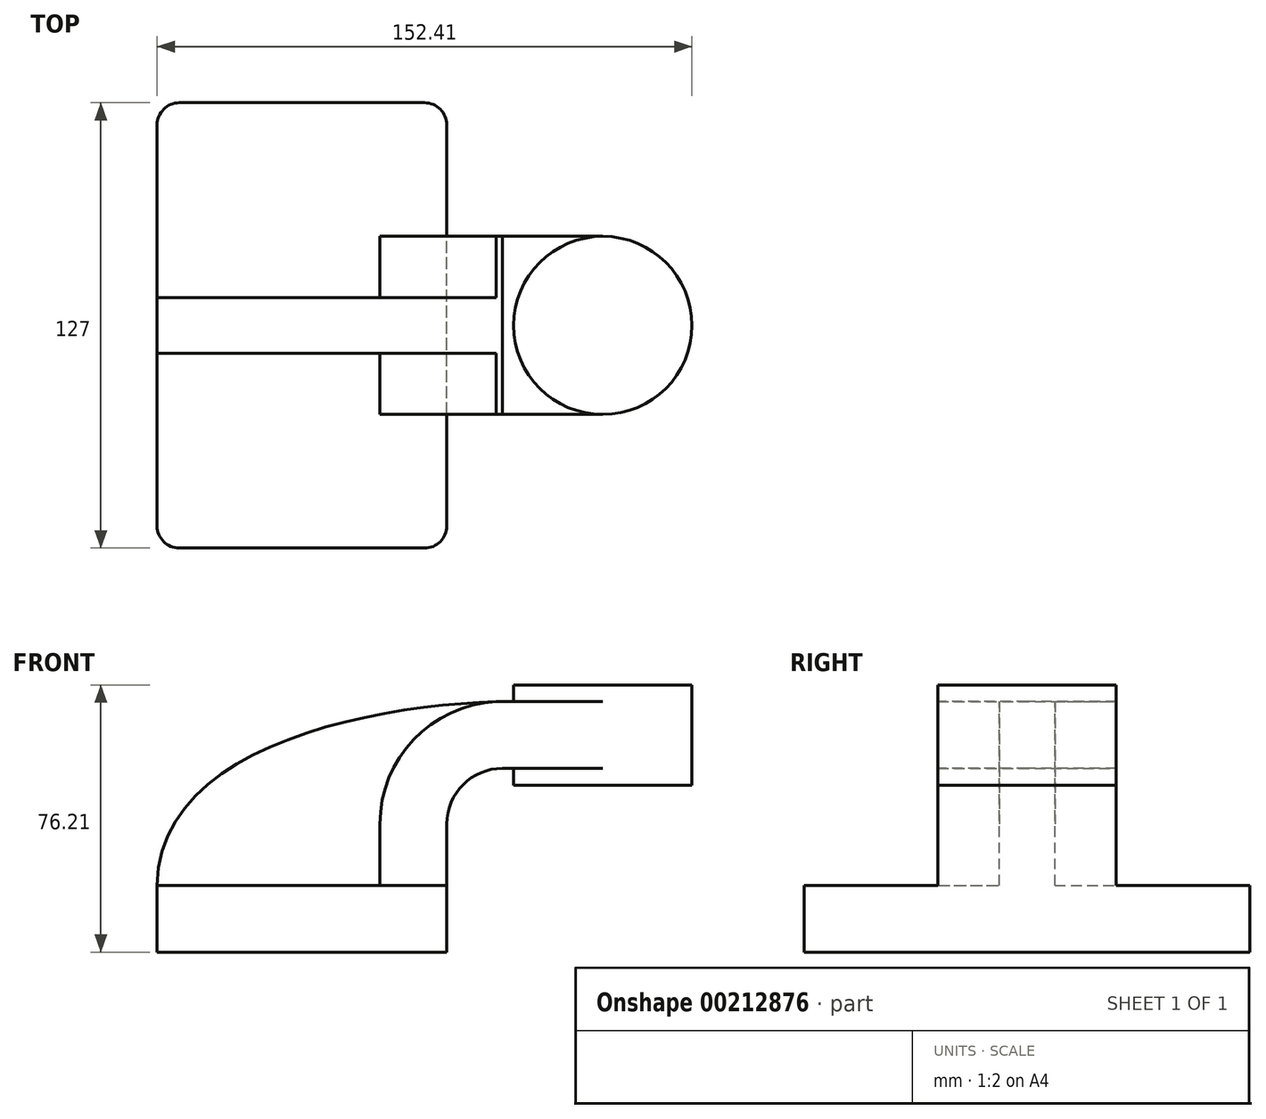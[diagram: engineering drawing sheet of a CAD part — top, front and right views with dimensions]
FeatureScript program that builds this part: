
annotation { "Feature Type Name" : "Feature", "Feature Type Description" : "" }
export const myFeature = defineFeature(function(context is Context, id is Id, definition is map)
    precondition{}
    {
        {
            var Q0;
            Q0=qCreatedBy(makeId("Front.planeOp"),FACE);
            var sketch = newSketch(context, id + "F0", { "sketchPlane" : qUnion([Q0])});
            skLineSegment(sketch, "E0.bottom", {"start": v(41.27, 9.53) * mm, "end": v(-41.28, 9.53) * mm});
            skLineSegment(sketch, "E0.top", {"start": v(41.28, -9.52) * mm, "end": v(-41.27, -9.52) * mm});
            skLineSegment(sketch, "E0.left", {"start": v(41.28, 9.53) * mm, "end": v(41.28, -9.52) * mm});
            skLineSegment(sketch, "E0.right", {"start": v(-41.28, 9.53) * mm, "end": v(-41.27, -9.52) * mm});
            skPoint(sketch, "E0.middle", {"position": v(0, 0) * mm});
            skLineSegment(sketch, "E1.bottom", {"start": v(111.12, 66.68) * mm, "end": v(60.32, 66.68) * mm});
            skLineSegment(sketch, "E1.top", {"start": v(111.13, 38.1) * mm, "end": v(60.32, 38.1) * mm});
            skLineSegment(sketch, "E1.left", {"start": v(111.12, 66.67) * mm, "end": v(111.13, 38.1) * mm});
            skLineSegment(sketch, "E1.right", {"start": v(60.32, 66.67) * mm, "end": v(60.32, 38.1) * mm});
            skPoint(sketch, "E1.middle", {"position": v(85.72, 52.39) * mm});
            skLineSegment(sketch, "E2", {"start": v(41.27, 9.53) * mm, "end": v(41.27, 27) * mm});
            skArc(sketch, "E3", {"start": v(41.27, 27) * mm, "mid": v(45.92, 38.23) * mm, "end": v(57.15, 42.88) * mm});
            skPoint(sketch, "E4.endSnap0", {"position": v(45.92, 38.23) * mm});
            skLineSegment(sketch, "E5", {"start": v(57.15, 42.88) * mm, "end": v(71.44, 42.88) * mm});
            skLineSegment(sketch, "E6.0", {"start": v(57.15, 61.93) * mm, "end": v(71.44, 61.93) * mm});
            skArc(sketch, "E6.1", {"start": v(22.23, 27) * mm, "mid": v(32.45, 51.7) * mm, "end": v(57.15, 61.93) * mm});
            skLineSegment(sketch, "E6.2", {"start": v(22.22, 9.53) * mm, "end": v(22.22, 27) * mm});
            skFitSpline(sketch, "E7", {"points": [v(-41.28, 9.52) * mm, v(57.15, 61.93) * mm], "startDerivative": vector(1.16, 119.88) * mm, "endDerivative": vector(109.6, 2.27) * mm});
            skLineSegment(sketch, "E8", {"start": v(85.72, 42.88) * mm, "end": v(85.72, 61.93) * mm});
            skLineSegment(sketch, "E9", {"start": v(71.44, 61.93) * mm, "end": v(85.72, 61.93) * mm});
            skLineSegment(sketch, "E10", {"start": v(71.44, 42.88) * mm, "end": v(85.72, 42.88) * mm});
            skLineSegment(sketch, "E11", {"start": v(85.72, 61.93) * mm, "end": v(85.72, 66.68) * mm});
            skLineSegment(sketch, "E12", {"start": v(85.72, 42.88) * mm, "end": v(85.72, 38.1) * mm});
            skSolve(sketch);
        }
        {
            var Q0;
            Q0=makeQuery(id+"F0.imprint","IMPRINT",FACE,{"disambiguationData":[TD([[makeQuery(id+"F0.imprint","IMPRINT",EDGE,{"derivedFrom":sQuery(id+"F0.wireOp",EDGE,"E0.top")}),-1.0]])]});
            extrude(context, id + "F1", {"entities" : qUnion([Q0]), "endBound" : BoundingType.SYMMETRIC, "depth" : 127 * mm});
        }
        {
            var Q0;
            {var subQ1=sQuery(id+"F0.wireOp",EDGE,"E2");Q0=makeQuery(id+"F0.imprint","IMPRINT",FACE,{"disambiguationData":[TD([[makeQuery(id+"F0.imprint","IMPRINT",EDGE,{"derivedFrom":subQ1}),1.0]])]});}
            var Q1;
            {var subQ0=sQuery(id+"F0.wireOp",EDGE,"ZMMKQKaz-5ktb-OAA6-osTW-7J0gWG6tDMML");Q1=makeQuery(id+"F0.imprint","IMPRINT",FACE,{"disambiguationData":[TD([[makeQuery(id+"F0.imprint","IMPRINT",EDGE,{"derivedFrom":subQ0}),-1.0]])]});}
            var Q2;
            Q2=makeQuery(id+"F0.imprint","IMPRINT",FACE,{"disambiguationData":[TD([[makeQuery(id+"F0.imprint","IMPRINT",EDGE,{"derivedFrom":sQuery(id+"F0.wireOp",EDGE,"E8")}),1.0]])]});
            extrude(context, id + "F2", {"entities" : qUnion([Q0, Q1, Q2]), "operationType" : NewBodyOperationType.ADD, "endBound" : BoundingType.SYMMETRIC, "depth" : 50.8 * mm});
        }
        {
            var Q0;
            {var subQ3=sQuery(id+"F0.wireOp",EDGE,"E6.2");Q0=makeQuery(id+"F0.imprint","IMPRINT",FACE,{"disambiguationData":[TD([[makeQuery(id+"F0.imprint","IMPRINT",EDGE,{"derivedFrom":subQ3}),1.0]])]});}
            extrude(context, id + "F3", {"entities" : qUnion([Q0]), "operationType" : NewBodyOperationType.ADD, "endBound" : BoundingType.SYMMETRIC, "depth" : 15.88 * mm});
        }
        {
            var Q0;
            {var subQ0=sQuery(id+"F0.wireOp",EDGE,"E1.left");Q0=makeQuery(id+"F0.imprint","IMPRINT",FACE,{"disambiguationData":[TD([[makeQuery(id+"F0.imprint","IMPRINT",EDGE,{"derivedFrom":subQ0}),-1.0]])]});}
            var Q1;
            Q1=sQuery(id+"F0.wireOp",EDGE,"E8");
            revolve(context, id + "F4", {"operationType" : NewBodyOperationType.ADD, "entities" : qUnion([Q0]), "axis" : qUnion([Q1]), "revolveType" : RevolveType.FULL});
        }
        {
            var Q0;
            Q0=makeQuery(id+"F1.opExtrude","CAP_EDGE",EDGE,{"disambiguationData":[OSD([sQuery(id+"F0.wireOp",EDGE,"E0.right")])],"isStart":false});
            var Q1;
            Q1=makeQuery(id+"F1.opExtrude","CAP_EDGE",EDGE,{"disambiguationData":[OSD([sQuery(id+"F0.wireOp",EDGE,"E0.left")])],"isStart":false});
            var Q2;
            Q2=makeQuery(id+"F1.opExtrude","CAP_EDGE",EDGE,{"disambiguationData":[OSD([sQuery(id+"F0.wireOp",EDGE,"E0.left")])],"isStart":true});
            var Q3;
            Q3=makeQuery(id+"F1.opExtrude","CAP_EDGE",EDGE,{"disambiguationData":[OSD([sQuery(id+"F0.wireOp",EDGE,"E0.right")])],"isStart":true});
            fillet(context, id + "F5", {"entities" : qUnion([Q0, Q1, Q2, Q3]), "radius" : 6.35 * mm, "tangentPropagation" : true, "allowEdgeOverflow" : false});
        }
    });
